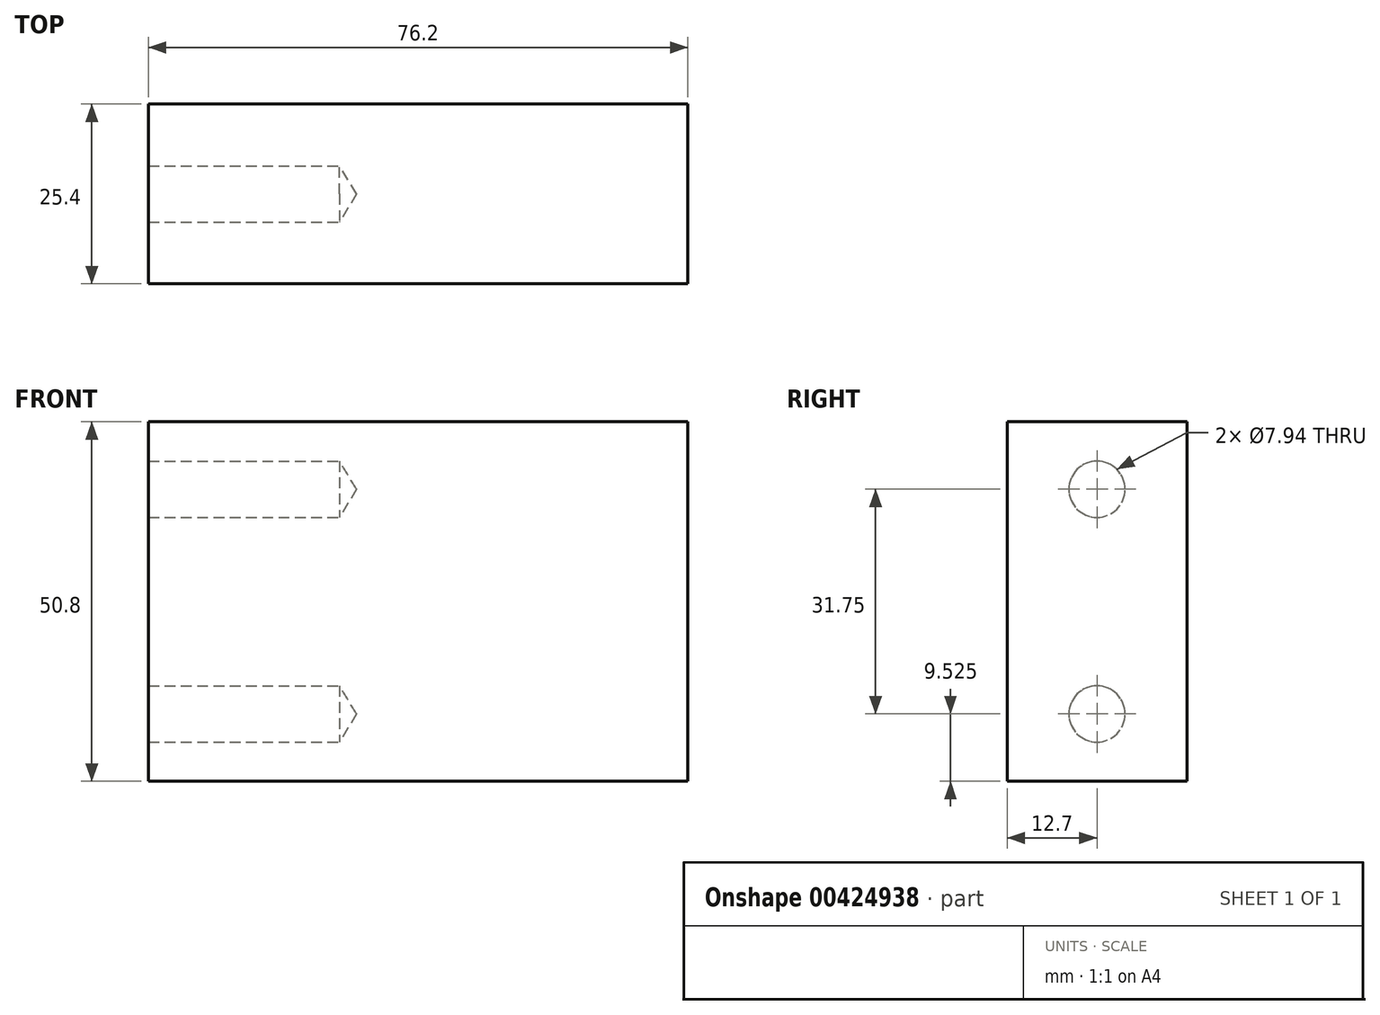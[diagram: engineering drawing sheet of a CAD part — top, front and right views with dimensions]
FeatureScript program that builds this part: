
annotation { "Feature Type Name" : "Feature", "Feature Type Description" : "" }
export const myFeature = defineFeature(function(context is Context, id is Id, definition is map)
    precondition{}
    {
        {
            var Q0;
            Q0=qCreatedBy(makeId("Front.planeOp"),FACE);
            var sketch = newSketch(context, id + "F0", { "sketchPlane" : qUnion([Q0])});
            skLineSegment(sketch, "E0.bottom", {"start": v(38.1, -25.4) * mm, "end": v(-38.1, -25.4) * mm});
            skLineSegment(sketch, "E0.top", {"start": v(38.1, 25.4) * mm, "end": v(-38.1, 25.4) * mm});
            skLineSegment(sketch, "E0.left", {"start": v(38.1, -25.4) * mm, "end": v(38.1, 25.4) * mm});
            skLineSegment(sketch, "E0.right", {"start": v(-38.1, -25.4) * mm, "end": v(-38.1, 25.4) * mm});
            skPoint(sketch, "E0.middle", {"position": v(0, 0) * mm});
            skSolve(sketch);
        }
        {
            var Q0;
            Q0=makeQuery(id+"F0.imprint","IMPRINT",FACE,{"disambiguationData":[TD([[makeQuery(id+"F0.imprint","IMPRINT",EDGE,{"derivedFrom":sQuery(id+"F0.wireOp",EDGE,"E0.bottom")}),-1.0]])]});
            extrude(context, id + "F1", {"entities" : qUnion([Q0]), "depth" : 25.4 * mm, "symmetric" : true});
        }
        {
            var Q0;
            Q0=makeQuery(id+"F1.opExtrude","SWEPT_FACE",FACE,{"disambiguationData":[OSD([sQuery(id+"F0.wireOp",EDGE,"E0.right")])]});
            var sketch = newSketch(context, id + "F2", { "sketchPlane" : qUnion([Q0])});
            skPoint(sketch, "E1", {"position": v(0, 15.88) * mm});
            skPoint(sketch, "E2", {"position": v(0, -15.88) * mm});
            skSolve(sketch);
        }
        {
            var Q0;
            Q0=sQuery(id+"F2.wireOp",VERTEX,"E1");
            var Q1;
            Q1=sQuery(id+"F2.wireOp",VERTEX,"E2");
            var Q2;
            Q2=makeQuery(id+"F1.opExtrude","SWEPT_BODY",BODY,{"disambiguationData":[OSD([sQuery(id+"F0.wireOp",EDGE,"E0.bottom"),sQuery(id+"F0.wireOp",EDGE,"E0.top"),sQuery(id+"F0.wireOp",EDGE,"E0.left"),sQuery(id+"F0.wireOp",EDGE,"E0.right")])]});
            hole(context, id + "F3", {"style" : HoleStyle.SIMPLE, "endStyle" : HoleEndStyle.BLIND, "standardTappedOrClearance" : lookupTablePath({ "standard" : "ANSI", "engagement" : "75%", "pitch" : "16 tpi", "size" : "3/8", "type" : "Tapped" }), "standardBlindInLast" : lookupTablePath({ "standard" : "ANSI", "engagement" : "75%", "pitch" : "16 tpi", "size" : "3/8", "type" : "Tapped" }), "holeDiameter" : 7.94 * mm, "showTappedDepth" : true, "holeDepth" : 27 * mm, "isTappedThrough" : true, "tappedDepth" : 22.24 * mm, "tapClearance" : 3, "locations" : qUnion([Q0, Q1]), "scope" : qUnion([Q2]), "majorDiameter" : 9.53 * mm, "startStyle" : HoleStartStyle.SKETCH});
        }
    });
